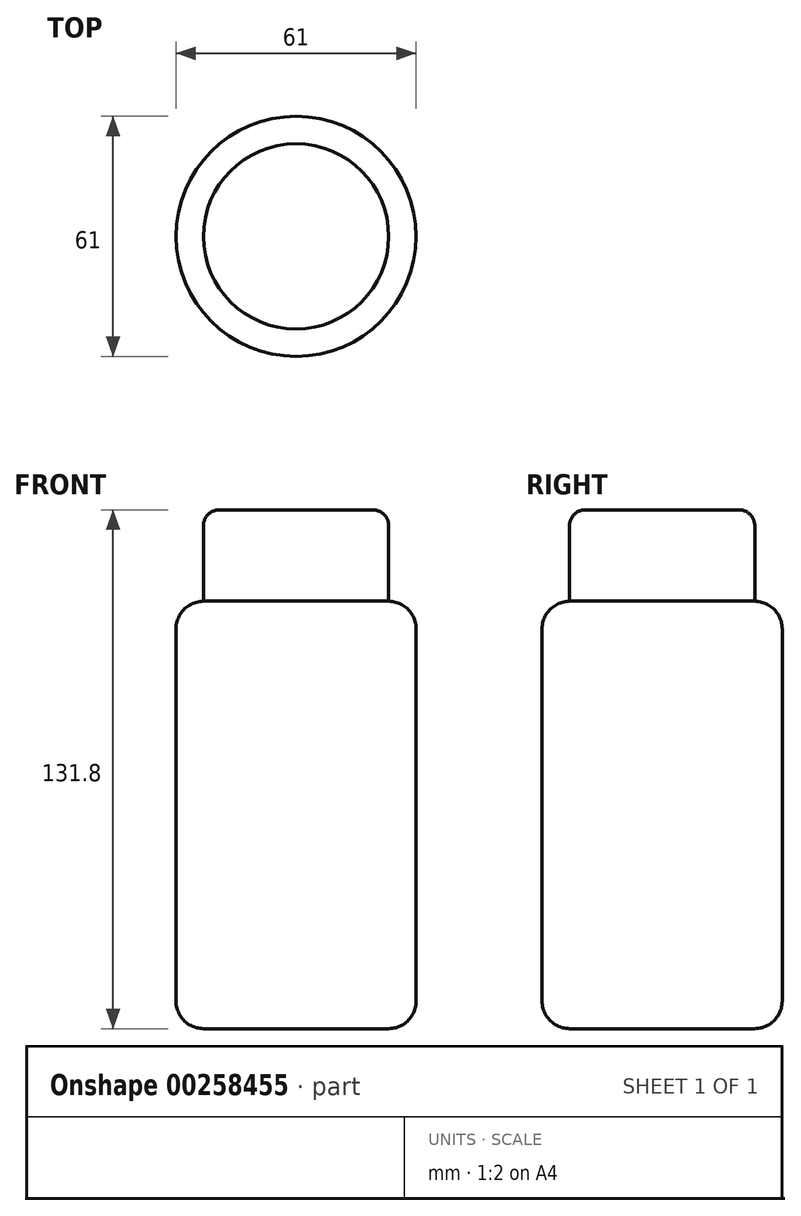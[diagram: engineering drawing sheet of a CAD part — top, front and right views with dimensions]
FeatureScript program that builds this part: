
annotation { "Feature Type Name" : "Feature", "Feature Type Description" : "" }
export const myFeature = defineFeature(function(context is Context, id is Id, definition is map)
    precondition{}
    {
        {
            var Q0;
            Q0=qCreatedBy(makeId("Front.planeOp"),FACE);
            var sketch = newSketch(context, id + "F0", { "sketchPlane" : qUnion([Q0])});
            skLineSegment(sketch, "E0.bottom", {"start": v(0, -54.3) * mm, "end": v(-30.5, -54.3) * mm});
            skLineSegment(sketch, "E0.top", {"start": v(0, 54.3) * mm, "end": v(-23.5, 54.3) * mm});
            skLineSegment(sketch, "E0.right", {"start": v(-30.5, -54.3) * mm, "end": v(-30.5, 47.3) * mm});
            skPoint(sketch, "E0.middle", {"position": v(0, 0) * mm});
            skPoint(sketch, "E1.visualSharp", {"position": v(-30.5, 54.3) * mm});
            skArc(sketch, "E1.filletArc", {"start": v(-23.5, 54.3) * mm, "mid": v(-28.45, 52.25) * mm, "end": v(-30.5, 47.3) * mm});
            skPoint(sketch, "E2.visualSharp", {"position": v(30.5, 54.3) * mm});
            skLineSegment(sketch, "E3", {"start": v(0, 54.3) * mm, "end": v(0, -54.3) * mm});
            skPoint(sketch, "E4.orphan", {"position": v(23.5, 54.3) * mm});
            skPoint(sketch, "E5.orphan", {"position": v(30.5, -54.3) * mm});
            skSolve(sketch);
        }
        {
            var Q0;
            Q0=makeQuery(id+"F0.imprint","IMPRINT",FACE,{"disambiguationData":[TD([[makeQuery(id+"F0.imprint","IMPRINT",EDGE,{"derivedFrom":sQuery(id+"F0.wireOp",EDGE,"E0.bottom")}),-1.0]])]});
            var Q1;
            Q1=sQuery(id+"F0.wireOp",EDGE,"E3");
            revolve(context, id + "F1", {"entities" : qUnion([Q0]), "axis" : qUnion([Q1]), "revolveType" : RevolveType.FULL});
        }
        {
            var Q0;
            Q0=makeQuery(id+"F1.opRevolve","SWEPT_EDGE",EDGE,{"disambiguationData":[OSD([sQuery(id+"F0.wireOp",EDGE,"E0.bottom"),sQuery(id+"F0.wireOp",EDGE,"E0.right")])]});
            fillet(context, id + "F2", {"entities" : qUnion([Q0]), "radius" : 7 * mm, "tangentPropagation" : true, "allowEdgeOverflow" : false});
        }
        {
            var Q0;
            Q0=makeQuery(id+"F1.opRevolve","SWEPT_FACE",FACE,{"disambiguationData":[OSD([sQuery(id+"F0.wireOp",EDGE,"E0.top")])]});
            var sketch = newSketch(context, id + "F3", { "sketchPlane" : qUnion([Q0])});
            skCircle(sketch, "E6", {"center": v(0, 0) * mm, "radius": 23.53 * mm});
            skSolve(sketch);
        }
        {
            var Q0;
            Q0=qSketchRegion(id+"F3",true);
            extrude(context, id + "F4", {"entities" : qUnion([Q0]), "operationType" : NewBodyOperationType.ADD, "depth" : 23.2 * mm});
        }
        {
            var Q0;
            Q0=makeQuery(id+"F4.opExtrude","CAP_EDGE",EDGE,{"disambiguationData":[OSD([sQuery(id+"F3.wireOp",EDGE,"E6")])],"isStart":false});
            fillet(context, id + "F5", {"entities" : qUnion([Q0]), "radius" : 4 * mm, "tangentPropagation" : true, "allowEdgeOverflow" : false});
        }
    });
